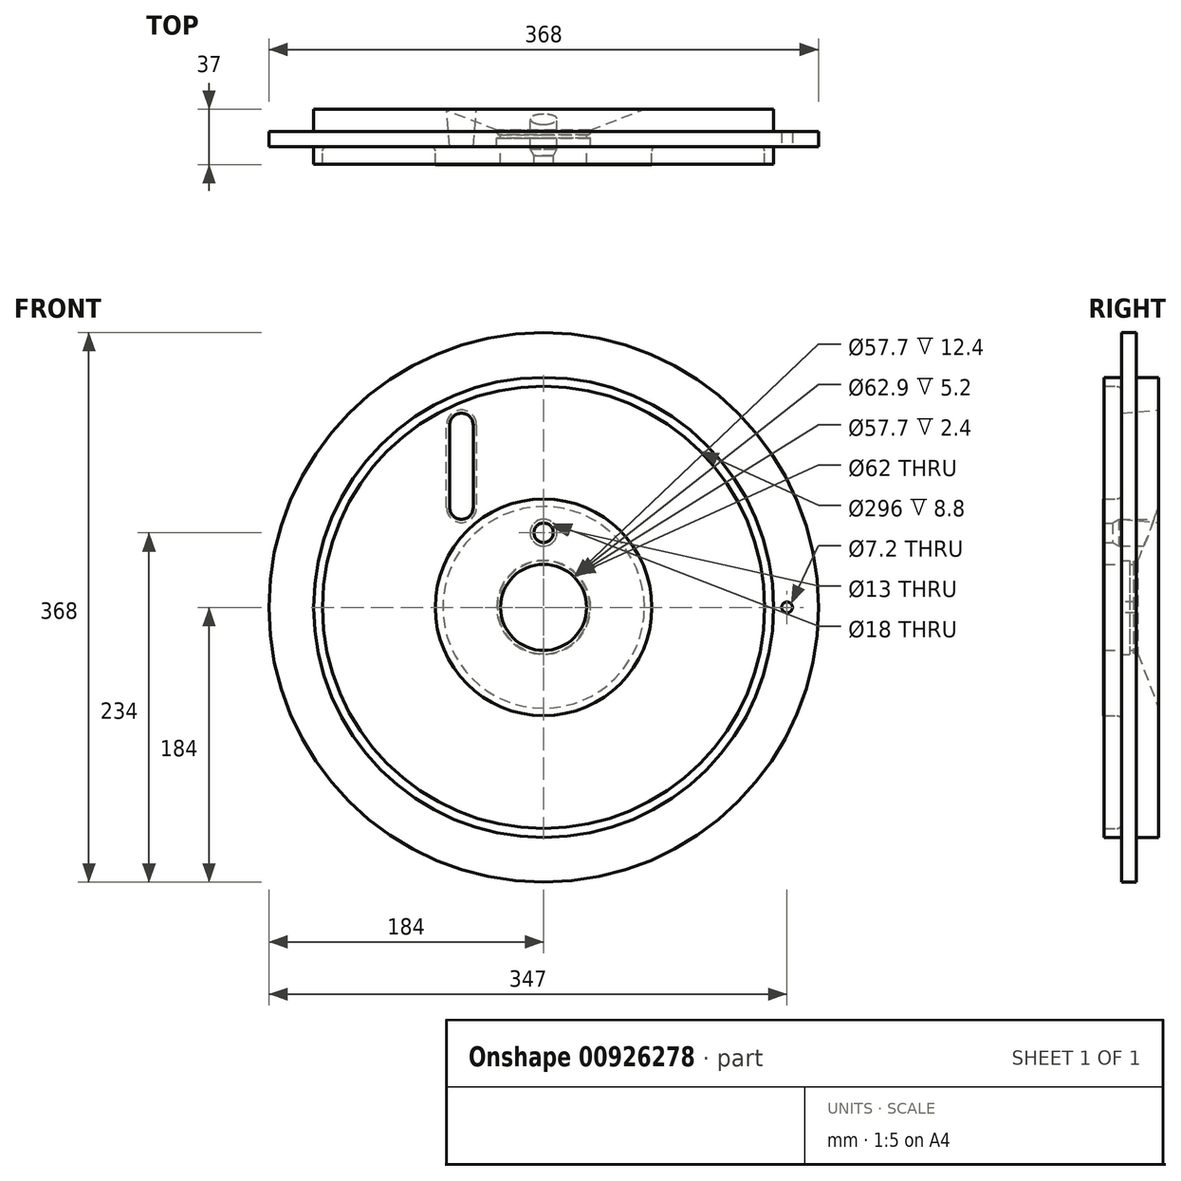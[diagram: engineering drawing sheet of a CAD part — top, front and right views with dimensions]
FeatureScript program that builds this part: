
annotation { "Feature Type Name" : "Feature", "Feature Type Description" : "" }
export const myFeature = defineFeature(function(context is Context, id is Id, definition is map)
    precondition{}
    {
        {
            var Q0;
            Q0=qCreatedBy(makeId("Top.planeOp"),FACE);
            var sketch = newSketch(context, id + "F0", { "sketchPlane" : qUnion([Q0])});
            skLineSegment(sketch, "E0", {"start": v(-72.5, 9) * mm, "end": v(-72.5, 0) * mm});
            skLineSegment(sketch, "E1", {"start": v(-72.5, 0) * mm, "end": v(-28.85, 0) * mm});
            skLineSegment(sketch, "E2", {"start": v(0, 47.35) * mm, "end": v(0, -31.33) * mm, "construction": true});
            skPoint(sketch, "E3.visualSharp", {"position": v(-72.5, 10) * mm});
            skLineSegment(sketch, "E4", {"start": v(-22.07, -0.9) * mm, "end": v(27.18, -0.9) * mm, "construction": true});
            skLineSegment(sketch, "E5", {"start": v(-154, 12) * mm, "end": v(-154, 0.2) * mm});
            skLineSegment(sketch, "E6", {"start": v(-154, 0.2) * mm, "end": v(-148, 0.2) * mm});
            skLineSegment(sketch, "E7", {"start": v(-148, 0.2) * mm, "end": v(-148, 9) * mm});
            skLineSegment(sketch, "E8", {"start": v(-28.85, 20) * mm, "end": v(-30, 20) * mm});
            skPoint(sketch, "E9.visualSharp", {"position": v(-35.7, 20) * mm});
            skLineSegment(sketch, "E10", {"start": v(-28.85, 20) * mm, "end": v(-28.85, 17.6) * mm});
            skLineSegment(sketch, "E11", {"start": v(-28.85, 17.6) * mm, "end": v(-31.45, 17.6) * mm});
            skLineSegment(sketch, "E12", {"start": v(-31.45, 17.6) * mm, "end": v(-31.45, 12.4) * mm});
            skLineSegment(sketch, "E13", {"start": v(-31.45, 12.4) * mm, "end": v(-28.85, 12.4) * mm});
            skLineSegment(sketch, "E14", {"start": v(-28.85, 12.4) * mm, "end": v(-28.85, 0) * mm});
            skLineSegment(sketch, "E15", {"start": v(-154, 12) * mm, "end": v(-184, 12) * mm});
            skLineSegment(sketch, "E16", {"start": v(-154, 37) * mm, "end": v(-67.5, 37) * mm});
            skPoint(sketch, "E17.visualSharp", {"position": v(-35, 23.4) * mm});
            skLineSegment(sketch, "E18", {"start": v(-145, 12) * mm, "end": v(-75.5, 12) * mm});
            skPoint(sketch, "E19.orphan", {"position": v(-148, 11.2) * mm});
            skPoint(sketch, "E20.visualSharp", {"position": v(-148, 12) * mm});
            skArc(sketch, "E20.filletArc", {"start": v(-145, 12) * mm, "mid": v(-147.12, 11.12) * mm, "end": v(-148, 9) * mm});
            skPoint(sketch, "E21.visualSharp", {"position": v(-72.5, 12) * mm});
            skArc(sketch, "E21.filletArc", {"start": v(-72.5, 9) * mm, "mid": v(-73.38, 11.12) * mm, "end": v(-75.5, 12) * mm});
            skLineSegment(sketch, "E22", {"start": v(-184, 12) * mm, "end": v(-184, 22) * mm});
            skLineSegment(sketch, "E23", {"start": v(-184, 22) * mm, "end": v(-154, 22) * mm});
            skLineSegment(sketch, "E24", {"start": v(-154, 22) * mm, "end": v(-154, 37) * mm});
            skLineSegment(sketch, "E25", {"start": v(-31, 23) * mm, "end": v(-67.5, 37) * mm});
            skLineSegment(sketch, "E26", {"start": v(-31, 23) * mm, "end": v(-31, 21) * mm});
            skPoint(sketch, "E27.visualSharp", {"position": v(-31, 20) * mm});
            skArc(sketch, "E27.filletArc", {"start": v(-31, 21) * mm, "mid": v(-30.7, 20.3) * mm, "end": v(-30, 20) * mm});
            skSolve(sketch);
        }
        {
            var Q0;
            Q0=makeQuery(id+"F0.imprint","IMPRINT",FACE,{"disambiguationData":[TD([[makeQuery(id+"F0.imprint","IMPRINT",EDGE,{"derivedFrom":sQuery(id+"F0.wireOp",EDGE,"E0")}),1.0]])]});
            var Q1;
            Q1=sQuery(id+"F0.wireOp",EDGE,"E2");
            revolve(context, id + "F1", {"surfaceOperationType" : NewSurfaceOperationType.NEW, "entities" : qUnion([Q0]), "axis" : qUnion([Q1]), "revolveType" : RevolveType.FULL});
        }
        {
            var Q0;
            Q0=qCreatedBy(makeId("Front.planeOp"),FACE);
            var sketch = newSketch(context, id + "F2", { "sketchPlane" : qUnion([Q0])});
            skCircle(sketch, "E28", {"center": v(163, 0) * mm, "radius": 3.6 * mm});
            skSolve(sketch);
        }
        {
            var Q0;
            Q0=qSketchRegion(id+"F2",true);
            extrude(context, id + "F3", {"entities" : qUnion([Q0]), "operationType" : NewBodyOperationType.REMOVE, "oppositeDirection" : true, "depth" : 50 * mm, "offsetDistance" : 25 * mm});
        }
        {
            var Q0;
            Q0=qCreatedBy(makeId("Right.planeOp"),FACE);
            var sketch = newSketch(context, id + "F4", { "sketchPlane" : qUnion([Q0])});
            skLineSegment(sketch, "E29", {"start": v(0, 50) * mm, "end": v(51.06, 50) * mm});
            skLineSegment(sketch, "E30", {"start": v(0, 56.5) * mm, "end": v(6, 56.5) * mm});
            skLineSegment(sketch, "E31", {"start": v(6, 56.5) * mm, "end": v(10.33, 59) * mm});
            skLineSegment(sketch, "E32", {"start": v(10.33, 59) * mm, "end": v(51.06, 59) * mm});
            skLineSegment(sketch, "E33", {"start": v(51.06, 59) * mm, "end": v(51.06, 50) * mm});
            skLineSegment(sketch, "E34", {"start": v(0, 50) * mm, "end": v(0, 56.5) * mm});
            skSolve(sketch);
        }
        {
            var Q0;
            Q0=qSketchRegion(id+"F4",true);
            var Q1;
            Q1=sQuery(id+"F4.wireOp",EDGE,"E29");
            revolve(context, id + "F5", {"operationType" : NewBodyOperationType.REMOVE, "surfaceOperationType" : NewSurfaceOperationType.NEW, "entities" : qUnion([Q0]), "axis" : qUnion([Q1]), "revolveType" : RevolveType.FULL, "oppositeDirection" : true});
        }
        {
            var Q0;
            Q0=makeQuery(id+"F1.opRevolve","SWEPT_FACE",FACE,{"disambiguationData":[OSD([sQuery(id+"F0.wireOp",EDGE,"E16")])]});
            var sketch = newSketch(context, id + "F6", { "sketchPlane" : qUnion([Q0])});
            skLineSegment(sketch, "E35", {"start": v(0, 0) * mm, "end": v(0, 203.33) * mm, "construction": true});
            skLineSegment(sketch, "E36", {"start": v(55, 203.33) * mm, "end": v(55, -15.97) * mm, "construction": true});
            skCircle(sketch, "E37", {"center": v(0, 0) * mm, "radius": 134 * mm, "construction": true});
            skCircle(sketch, "E38", {"center": v(0, 0) * mm, "radius": 86.5 * mm, "construction": true});
            skLineSegment(sketch, "E39", {"start": v(65, 122.2) * mm, "end": v(65, 66.76) * mm});
            skLineSegment(sketch, "E40", {"start": v(45, 66.76) * mm, "end": v(45, 122.2) * mm});
            skPoint(sketch, "E41.orphan", {"position": v(45, 138.62) * mm});
            skPoint(sketch, "E42.orphan", {"position": v(65, 138.62) * mm});
            skArc(sketch, "E43", {"start": v(45, 66.76) * mm, "mid": v(55, 56.76) * mm, "end": v(65, 66.76) * mm});
            skArc(sketch, "E44", {"start": v(65, 122.2) * mm, "mid": v(55, 132.2) * mm, "end": v(45, 122.2) * mm});
            skSolve(sketch);
        }
        {
            var Q0;
            Q0=qSketchRegion(id+"F6",true);
            extrude(context, id + "F7", {"entities" : qUnion([Q0]), "operationType" : NewBodyOperationType.REMOVE, "endBound" : BoundingType.THROUGH_ALL, "oppositeDirection" : true, "depth" : 25 * mm, "offsetDistance" : 25 * mm, "hasDraft" : true, "draftAngle" : 5 * degree, "draftPullDirection" : true});
        }
    });
